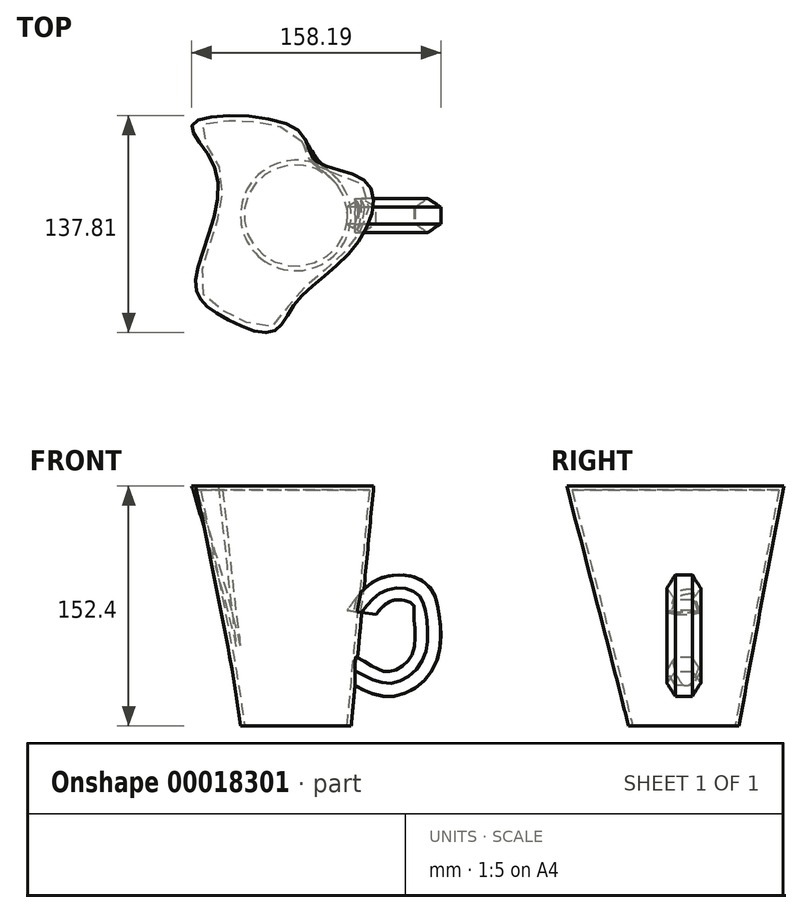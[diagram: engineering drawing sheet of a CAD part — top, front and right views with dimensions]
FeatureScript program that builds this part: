
annotation { "Feature Type Name" : "Feature", "Feature Type Description" : "" }
export const myFeature = defineFeature(function(context is Context, id is Id, definition is map)
    precondition{}
    {
        {
            var Q0;
            Q0=qCreatedBy(makeId("Top.planeOp"),FACE);
            var sketch = newSketch(context, id + "F0", { "sketchPlane" : qUnion([Q0])});
            skCircle(sketch, "E0", {"center": v(0, 0) * mm, "radius": 35.11 * mm});
            skSolve(sketch);
        }
        {
            var Q0;
            Q0=makeQuery(id+"F0.imprint","IMPRINT",FACE,{"disambiguationData":[TD([[makeQuery(id+"F0.imprint","IMPRINT",EDGE,{"derivedFrom":sQuery(id+"F0.wireOp",EDGE,"E0")}),1.0]])]});
            cPlane(context, id + "F1", {"entities" : qUnion([Q0]), "cplaneType" : CPlaneType.OFFSET, "offset" : 152.4 * mm, "width" : 152.4 * mm, "height" : 152.4 * mm});
        }
        {
            var Q0;
            Q0=qCreatedBy(id+"F1.planeOp",FACE);
            var sketch = newSketch(context, id + "F2", { "sketchPlane" : qUnion([Q0])});
            skFitSpline(sketch, "E1", {"points": [v(-50.46, -61.84) * mm, v(-63.67, -41.73) * mm, v(-50.32, 27.08) * mm, v(-65.3, 58.28) * mm, v(0, 55.18) * mm, v(12.43, 34.97) * mm, v(45.66, 20.38) * mm, v(38.92, -17.9) * mm, v(0, -55.32) * mm, v(-15.29, -73.86) * mm, v(-50.46, -61.84) * mm]});
            skSolve(sketch);
        }
        {
            var Q0;
            Q0=makeQuery(id+"F2.imprint","IMPRINT",FACE,{"disambiguationData":[TD([[makeQuery(id+"F2.imprint","IMPRINT",EDGE,{"derivedFrom":sQuery(id+"F2.wireOp",EDGE,"E1")}),-1.0]])]});
            var Q1;
            Q1=makeQuery(id+"F0.imprint","IMPRINT",FACE,{"disambiguationData":[TD([[makeQuery(id+"F0.imprint","IMPRINT",EDGE,{"derivedFrom":sQuery(id+"F0.wireOp",EDGE,"E0")}),1.0]])]});
            loft(context, id + "F3", {"sheetProfilesArray" : [{ "sheetProfileEntities" : qUnion([Q0]) }, { "sheetProfileEntities" : qUnion([Q1]) }]});
        }
        {
            var Q0;
            Q0=makeQuery(id+"F3.opLoft","CAP_FACE",FACE,{"disambiguationData":[OSD([makeQuery(id+"F0.imprint","IMPRINT",FACE,{"disambiguationData":[TD([[makeQuery(id+"F0.imprint","IMPRINT",EDGE,{"derivedFrom":sQuery(id+"F0.wireOp",EDGE,"E0")}),1.0]])]})])],"isStart":true});
            shell(context, id + "F4", {"entities" : qUnion([Q0]), "thickness" : 2.54 * mm});
        }
        {
            var Q0;
            Q0=qCreatedBy(makeId("Right.planeOp"),FACE);
            cPlane(context, id + "F5", {"entities" : qUnion([Q0]), "cplaneType" : CPlaneType.OFFSET, "offset" : 38.1 * mm, "width" : 152.4 * mm, "height" : 152.4 * mm});
        }
        {
            var Q0;
            Q0=qCreatedBy(id+"F5.planeOp",FACE);
            var sketch = newSketch(context, id + "F6", { "sketchPlane" : qUnion([Q0])});
            skCircle(sketch, "E2.cCircle", {"center": v(0, 34.72) * mm, "radius": 9.3 * mm, "construction": true});
            skLineSegment(sketch, "E2.0", {"start": v(-5.37, 44.02) * mm, "end": v(5.37, 44.02) * mm});
            skLineSegment(sketch, "E2.1", {"start": v(5.37, 44.02) * mm, "end": v(10.74, 34.72) * mm});
            skLineSegment(sketch, "E2.2", {"start": v(10.74, 34.72) * mm, "end": v(5.37, 25.42) * mm});
            skLineSegment(sketch, "E2.3", {"start": v(5.37, 25.42) * mm, "end": v(-5.37, 25.42) * mm});
            skLineSegment(sketch, "E2.4", {"start": v(-5.37, 25.42) * mm, "end": v(-10.74, 34.72) * mm});
            skLineSegment(sketch, "E2.5", {"start": v(-10.74, 34.72) * mm, "end": v(-5.37, 44.02) * mm});
            skPoint(sketch, "E2.0.midPoint", {"position": v(0, 44.02) * mm});
            skSolve(sketch);
        }
        {
            var Q0;
            Q0=qCreatedBy(makeId("Front.planeOp"),FACE);
            var sketch = newSketch(context, id + "F7", { "sketchPlane" : qUnion([Q0])});
            skFitSpline(sketch, "E3", {"points": [v(37.5, 35.04) * mm, v(60.67, 27.17) * mm, v(80.4, 41.54) * mm, v(82.94, 69.35) * mm, v(75.97, 84.93) * mm, v(56.53, 85.84) * mm, v(41.58, 72.03) * mm], "startDerivative": vector(131.3, -73.76) * mm, "endDerivative": vector(-80.1, -104.84) * mm});
            skSolve(sketch);
        }
        {
            var Q0;
            Q0=makeQuery(id+"F6.imprint","IMPRINT",FACE,{"disambiguationData":[TD([[makeQuery(id+"F6.imprint","IMPRINT",EDGE,{"derivedFrom":sQuery(id+"F6.wireOp",EDGE,"E2.0")}),-1.0]])]});
            var Q1;
            Q1=sQuery(id+"F7.wireOp",EDGE,"E3");
            sweep(context, id + "F8", {"operationType" : NewBodyOperationType.ADD, "profiles" : qUnion([Q0]), "path" : qUnion([Q1])});
        }
    });
